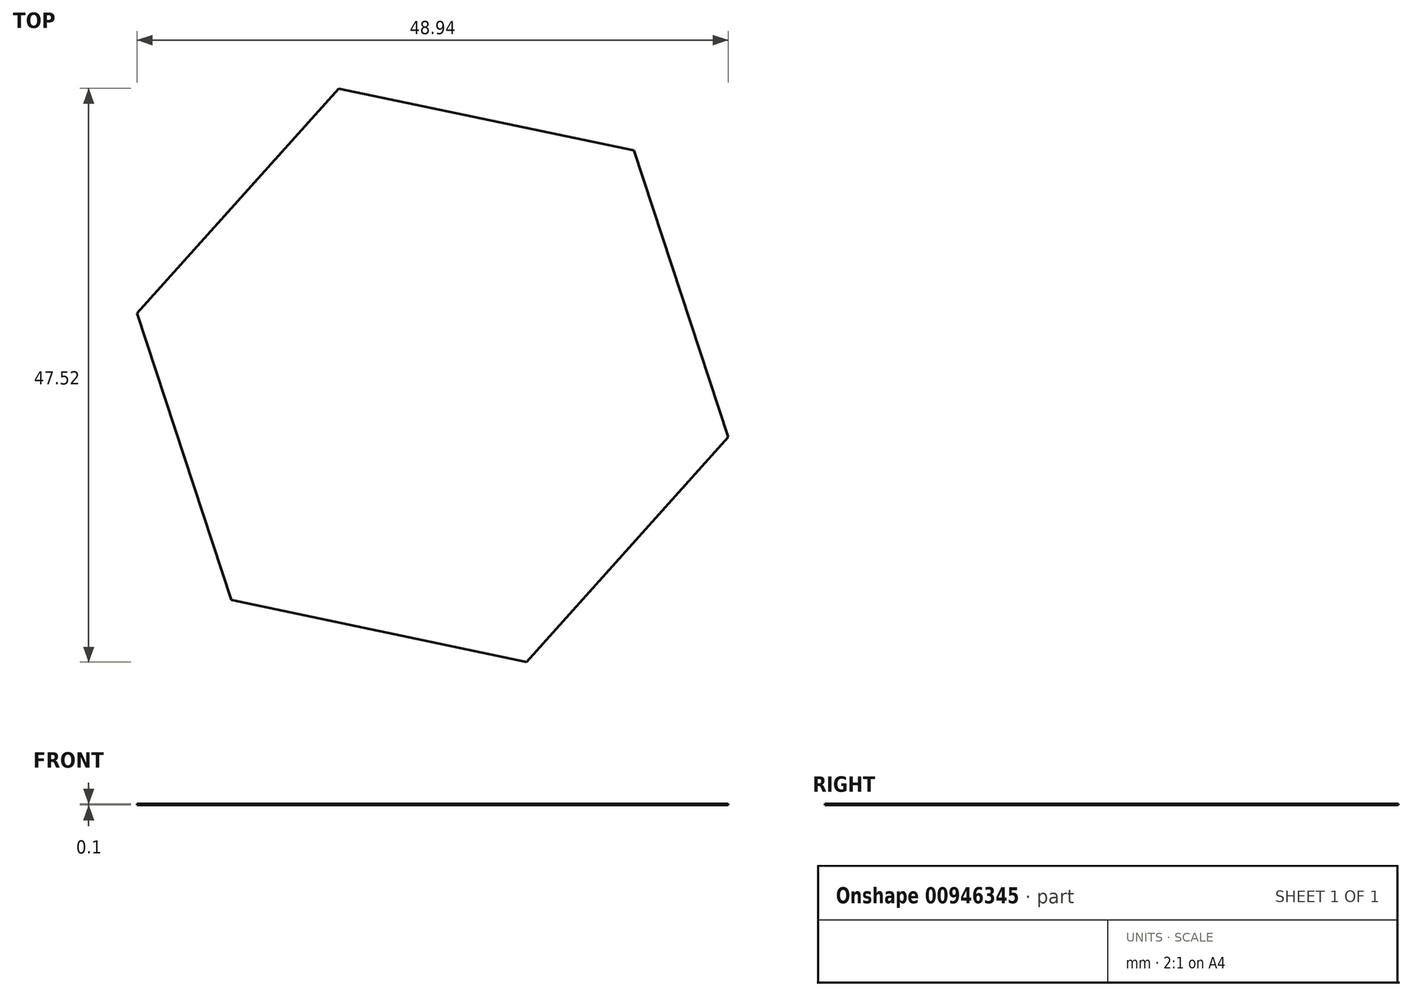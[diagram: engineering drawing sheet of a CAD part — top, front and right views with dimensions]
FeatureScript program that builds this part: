
annotation { "Feature Type Name" : "Feature", "Feature Type Description" : "" }
export const myFeature = defineFeature(function(context is Context, id is Id, definition is map)
    precondition{}
    {
        {
            var Q0;
            Q0=qCreatedBy(makeId("Top.planeOp"),FACE);
            var sketch = newSketch(context, id + "F0", { "sketchPlane" : qUnion([Q0])});
            skCircle(sketch, "E0.cCircle", {"center": v(0, 0) * mm, "radius": 21.65 * mm, "construction": true});
            skLineSegment(sketch, "E0.0", {"start": v(24.47, -5.13) * mm, "end": v(7.8, -23.76) * mm});
            skLineSegment(sketch, "E0.1", {"start": v(7.8, -23.76) * mm, "end": v(-16.68, -18.62) * mm});
            skLineSegment(sketch, "E0.2", {"start": v(-16.68, -18.62) * mm, "end": v(-24.47, 5.13) * mm});
            skLineSegment(sketch, "E0.3", {"start": v(-24.47, 5.13) * mm, "end": v(-7.8, 23.76) * mm});
            skLineSegment(sketch, "E0.4", {"start": v(-7.8, 23.76) * mm, "end": v(16.68, 18.62) * mm});
            skLineSegment(sketch, "E0.5", {"start": v(16.68, 18.62) * mm, "end": v(24.47, -5.13) * mm});
            skPoint(sketch, "E0.0.midPoint", {"position": v(16.13, -14.44) * mm});
            skSolve(sketch);
        }
        {
            var Q0;
            Q0=makeQuery(id+"F0.imprint","IMPRINT",FACE,{"disambiguationData":[TD([[makeQuery(id+"F0.imprint","IMPRINT",EDGE,{"derivedFrom":sQuery(id+"F0.wireOp",EDGE,"E0.0")}),-1.0]])]});
            extrude(context, id + "F1", {"entities" : qUnion([Q0]), "depth" : 0.1 * mm, "offsetDistance" : 25 * mm});
        }
    });
